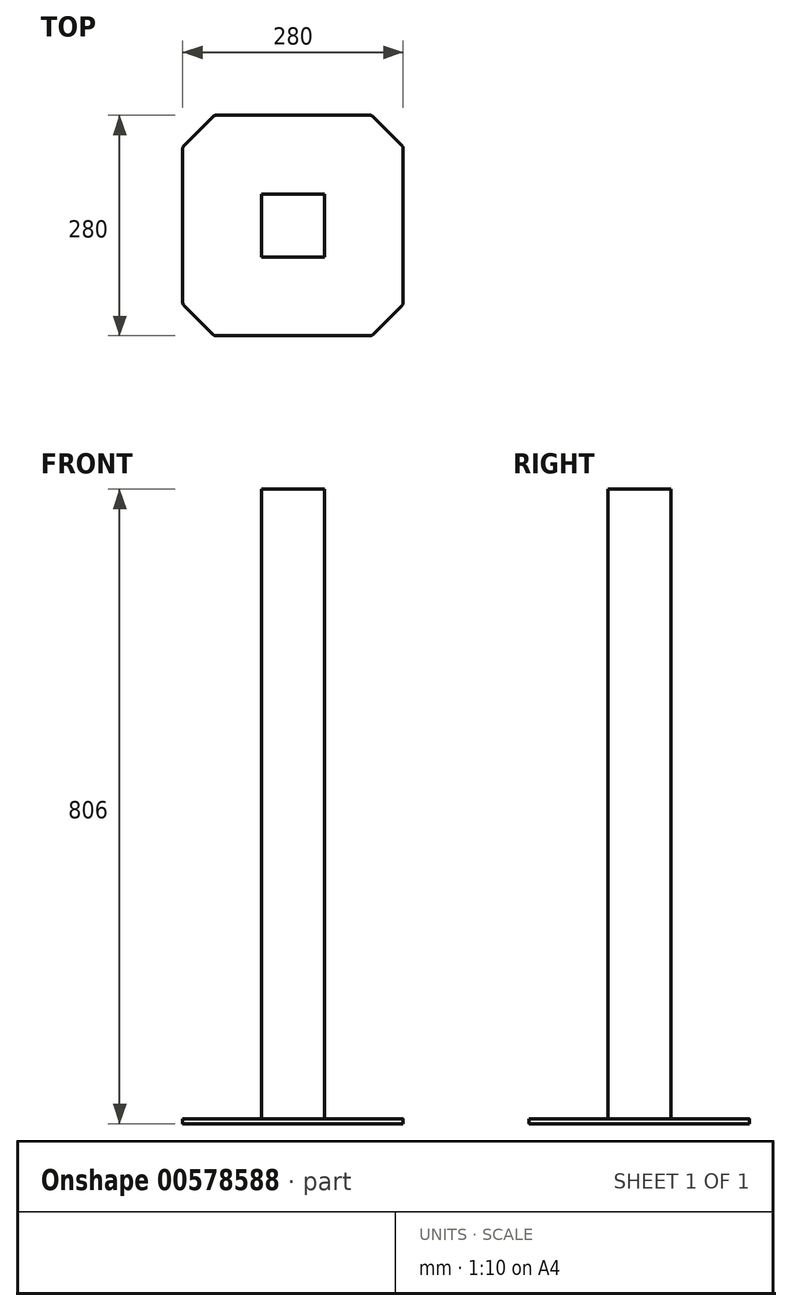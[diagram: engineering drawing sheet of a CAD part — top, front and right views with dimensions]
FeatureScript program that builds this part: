
annotation { "Feature Type Name" : "Feature", "Feature Type Description" : "" }
export const myFeature = defineFeature(function(context is Context, id is Id, definition is map)
    precondition{}
    {
        {
            var Q0;
            Q0=qCreatedBy(makeId("Top.planeOp"),FACE);
            var sketch = newSketch(context, id + "F0", { "sketchPlane" : qUnion([Q0])});
            skLineSegment(sketch, "E0.bottom", {"start": v(-40, 40) * mm, "end": v(40, 40) * mm});
            skLineSegment(sketch, "E0.top", {"start": v(-40, -40) * mm, "end": v(40, -40) * mm});
            skLineSegment(sketch, "E0.left", {"start": v(-40, 40) * mm, "end": v(-40, -40) * mm});
            skLineSegment(sketch, "E0.right", {"start": v(40, 40) * mm, "end": v(40, -40) * mm});
            skLineSegment(sketch, "E1", {"start": v(0, 70.9) * mm, "end": v(0, -85.85) * mm, "construction": true});
            skLineSegment(sketch, "E2", {"start": v(-71.93, 0) * mm, "end": v(108.98, 0) * mm, "construction": true});
            skSolve(sketch);
        }
        {
            var Q0;
            Q0 = qSketchRegion(id + "F0", true);
            extrude(context, id + "F1", {"entities" : qUnion([Q0]), "depth" : 800 * mm, "offsetDistance" : 25 * mm});
        }
        {
            var Q0;
            Q0=makeQuery(id+"F1.opExtrude","CAP_FACE",FACE,{"disambiguationData":[OSD([sQuery(id+"F0.wireOp",EDGE,"E0.bottom"),sQuery(id+"F0.wireOp",EDGE,"E0.top"),sQuery(id+"F0.wireOp",EDGE,"E0.left"),sQuery(id+"F0.wireOp",EDGE,"E0.right")])],"isStart":true});
            var sketch = newSketch(context, id + "F2", { "sketchPlane" : qUnion([Q0])});
            skLineSegment(sketch, "E3.0", {"start": v(-140, 140) * mm, "end": v(-140, -140) * mm});
            skLineSegment(sketch, "E3.1", {"start": v(140, 140) * mm, "end": v(-140, 140) * mm});
            skLineSegment(sketch, "E3.2", {"start": v(140, -140) * mm, "end": v(140, 140) * mm});
            skLineSegment(sketch, "E3.3", {"start": v(-140, -140) * mm, "end": v(140, -140) * mm});
            skSolve(sketch);
        }
        {
            var Q0;
            Q0 = qSketchRegion(id + "F2", true);
            extrude(context, id + "F3", {"entities" : qUnion([Q0]), "operationType" : NewBodyOperationType.ADD, "depth" : 6 * mm, "offsetDistance" : 25 * mm});
        }
        {
            var Q0;
            Q0=makeQuery(id+"F3.opExtrude","SWEPT_EDGE",EDGE,{"disambiguationData":[OSD([sQuery(id+"F2.wireOp",EDGE,"E3.1"),sQuery(id+"F2.wireOp",EDGE,"E3.2")])]});
            var Q1;
            Q1=makeQuery(id+"F3.opExtrude","SWEPT_EDGE",EDGE,{"disambiguationData":[OSD([sQuery(id+"F2.wireOp",EDGE,"E3.2"),sQuery(id+"F2.wireOp",EDGE,"E3.3")])]});
            var Q2;
            Q2=makeQuery(id+"F3.opExtrude","SWEPT_EDGE",EDGE,{"disambiguationData":[OSD([sQuery(id+"F2.wireOp",EDGE,"E3.0"),sQuery(id+"F2.wireOp",EDGE,"E3.3")])]});
            var Q3;
            Q3=makeQuery(id+"F3.opExtrude","SWEPT_EDGE",EDGE,{"disambiguationData":[OSD([sQuery(id+"F2.wireOp",EDGE,"E3.0"),sQuery(id+"F2.wireOp",EDGE,"E3.1")])]});
            chamfer(context, id + "F4", {"entities" : qUnion([Q0, Q1, Q2, Q3]), "width" : 40 * mm, "tangentPropagation" : true});
        }
        {
            var Q0;
            {var subQ0=sQuery(id+"F2.wireOp",EDGE,"E3.2");Q0=makeQuery(id+"F4.opChamfer","BLEND_EDGE",EDGE,{"blendedFrom":[makeQuery(id+"F3.opExtrude","SWEPT_EDGE",EDGE,{"disambiguationData":[OSD([sQuery(id+"F2.wireOp",EDGE,"E3.1"),subQ0])]}),makeQuery(id+"F3.opExtrude","SWEPT_FACE",FACE,{"disambiguationData":[OSD([subQ0])]})],"blendedInto":[makeQuery(id+"F3.opExtrude","SWEPT_FACE",FACE,{"disambiguationData":[OSD([subQ0])]})]});}
            var Q1;
            {var subQ0=sQuery(id+"F2.wireOp",EDGE,"E3.1");Q1=makeQuery(id+"F4.opChamfer","BLEND_EDGE",EDGE,{"blendedFrom":[makeQuery(id+"F3.opExtrude","SWEPT_EDGE",EDGE,{"disambiguationData":[OSD([subQ0,sQuery(id+"F2.wireOp",EDGE,"E3.2")])]}),makeQuery(id+"F3.opExtrude","SWEPT_FACE",FACE,{"disambiguationData":[OSD([subQ0])]})],"blendedInto":[makeQuery(id+"F3.opExtrude","SWEPT_FACE",FACE,{"disambiguationData":[OSD([subQ0])]})]});}
            var Q2;
            {var subQ0=sQuery(id+"F2.wireOp",EDGE,"E3.2");Q2=makeQuery(id+"F4.opChamfer","BLEND_EDGE",EDGE,{"blendedFrom":[makeQuery(id+"F3.opExtrude","SWEPT_EDGE",EDGE,{"disambiguationData":[OSD([subQ0,sQuery(id+"F2.wireOp",EDGE,"E3.3")])]}),makeQuery(id+"F3.opExtrude","SWEPT_FACE",FACE,{"disambiguationData":[OSD([subQ0])]})],"blendedInto":[makeQuery(id+"F3.opExtrude","SWEPT_FACE",FACE,{"disambiguationData":[OSD([subQ0])]})]});}
            var Q3;
            {var subQ0=sQuery(id+"F2.wireOp",EDGE,"E3.3");Q3=makeQuery(id+"F4.opChamfer","BLEND_EDGE",EDGE,{"blendedFrom":[makeQuery(id+"F3.opExtrude","SWEPT_EDGE",EDGE,{"disambiguationData":[OSD([sQuery(id+"F2.wireOp",EDGE,"E3.2"),subQ0])]}),makeQuery(id+"F3.opExtrude","SWEPT_FACE",FACE,{"disambiguationData":[OSD([subQ0])]})],"blendedInto":[makeQuery(id+"F3.opExtrude","SWEPT_FACE",FACE,{"disambiguationData":[OSD([subQ0])]})]});}
            var Q4;
            {var subQ0=sQuery(id+"F2.wireOp",EDGE,"E3.3");Q4=makeQuery(id+"F4.opChamfer","BLEND_EDGE",EDGE,{"blendedFrom":[makeQuery(id+"F3.opExtrude","SWEPT_EDGE",EDGE,{"disambiguationData":[OSD([sQuery(id+"F2.wireOp",EDGE,"E3.0"),subQ0])]}),makeQuery(id+"F3.opExtrude","SWEPT_FACE",FACE,{"disambiguationData":[OSD([subQ0])]})],"blendedInto":[makeQuery(id+"F3.opExtrude","SWEPT_FACE",FACE,{"disambiguationData":[OSD([subQ0])]})]});}
            var Q5;
            {var subQ0=sQuery(id+"F2.wireOp",EDGE,"E3.0");Q5=makeQuery(id+"F4.opChamfer","BLEND_EDGE",EDGE,{"blendedFrom":[makeQuery(id+"F3.opExtrude","SWEPT_EDGE",EDGE,{"disambiguationData":[OSD([subQ0,sQuery(id+"F2.wireOp",EDGE,"E3.3")])]}),makeQuery(id+"F3.opExtrude","SWEPT_FACE",FACE,{"disambiguationData":[OSD([subQ0])]})],"blendedInto":[makeQuery(id+"F3.opExtrude","SWEPT_FACE",FACE,{"disambiguationData":[OSD([subQ0])]})]});}
            var Q6;
            {var subQ0=sQuery(id+"F2.wireOp",EDGE,"E3.1");Q6=makeQuery(id+"F4.opChamfer","BLEND_EDGE",EDGE,{"blendedFrom":[makeQuery(id+"F3.opExtrude","SWEPT_EDGE",EDGE,{"disambiguationData":[OSD([sQuery(id+"F2.wireOp",EDGE,"E3.0"),subQ0])]}),makeQuery(id+"F3.opExtrude","SWEPT_FACE",FACE,{"disambiguationData":[OSD([subQ0])]})],"blendedInto":[makeQuery(id+"F3.opExtrude","SWEPT_FACE",FACE,{"disambiguationData":[OSD([subQ0])]})]});}
            var Q7;
            {var subQ0=sQuery(id+"F2.wireOp",EDGE,"E3.0");Q7=makeQuery(id+"F4.opChamfer","BLEND_EDGE",EDGE,{"blendedFrom":[makeQuery(id+"F3.opExtrude","SWEPT_EDGE",EDGE,{"disambiguationData":[OSD([subQ0,sQuery(id+"F2.wireOp",EDGE,"E3.1")])]}),makeQuery(id+"F3.opExtrude","SWEPT_FACE",FACE,{"disambiguationData":[OSD([subQ0])]})],"blendedInto":[makeQuery(id+"F3.opExtrude","SWEPT_FACE",FACE,{"disambiguationData":[OSD([subQ0])]})]});}
            fillet(context, id + "F5", {"entities" : qUnion([Q0, Q1, Q2, Q3, Q4, Q5, Q6, Q7]), "radius" : 5 * mm, "tangentPropagation" : true, "allowEdgeOverflow" : false});
        }
    });
